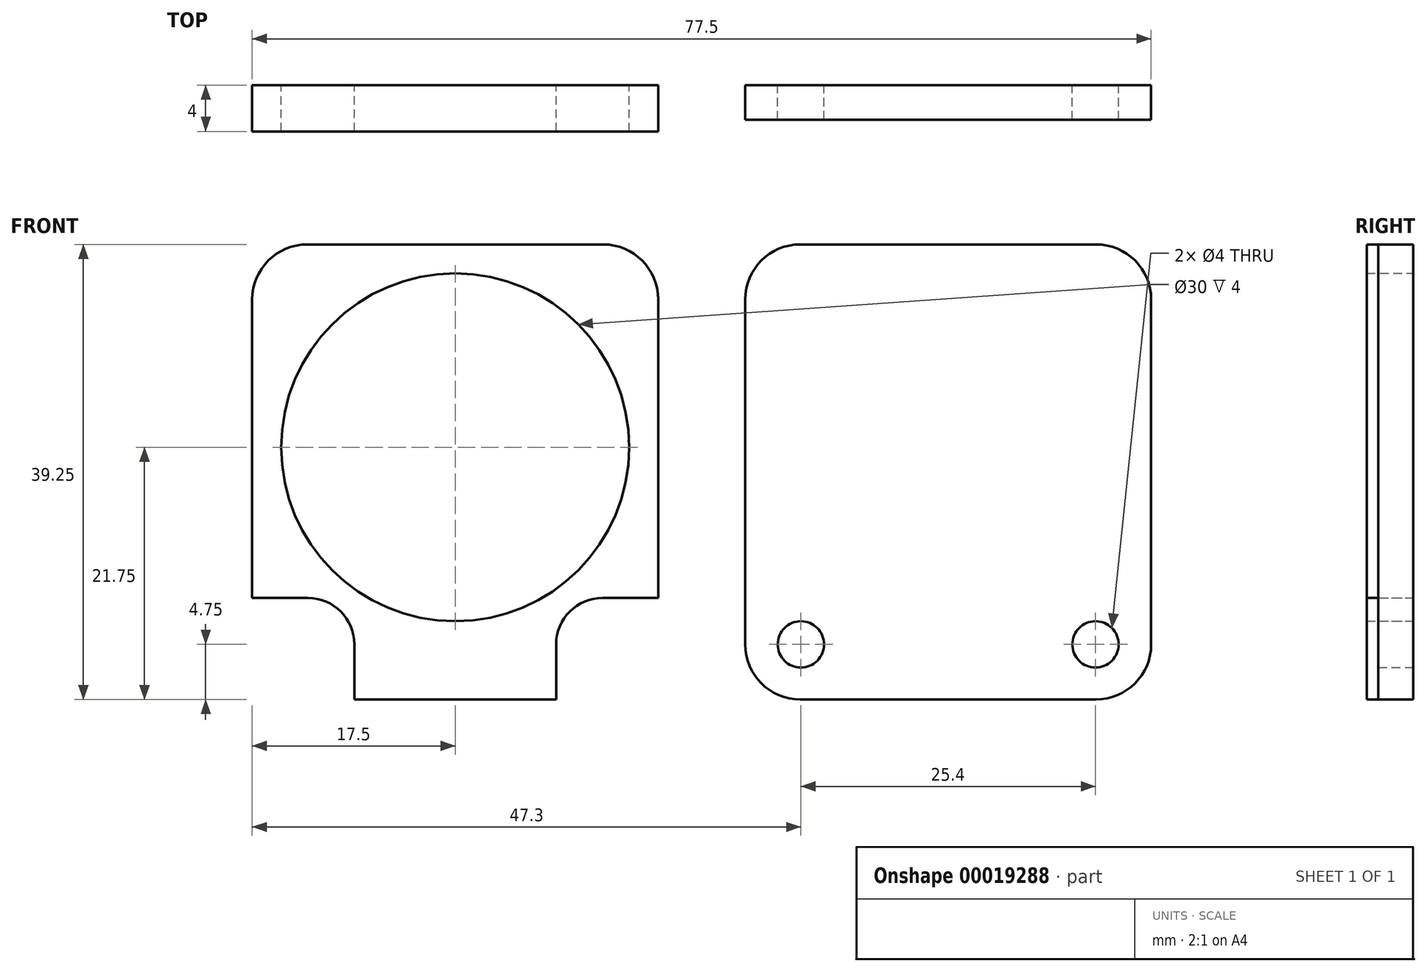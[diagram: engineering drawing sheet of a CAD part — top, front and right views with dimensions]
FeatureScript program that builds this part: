
annotation { "Feature Type Name" : "Feature", "Feature Type Description" : "" }
export const myFeature = defineFeature(function(context is Context, id is Id, definition is map)
    precondition{}
    {
        {
            var Q0;
            Q0=qCreatedBy(makeId("Front.planeOp"),FACE);
            var sketch = newSketch(context, id + "F0", { "sketchPlane" : qUnion([Q0])});
            skArc(sketch, "E0", {"start": v(12.7, 4) * mm, "mid": v(9.87, 2.83) * mm, "end": v(8.7, 0) * mm});
            skLineSegment(sketch, "E1", {"start": v(-12.7, 0) * mm, "end": v(12.7, 0) * mm, "construction": true});
            skLineSegment(sketch, "E2.bottom", {"start": v(-17.5, 2) * mm, "end": v(17.5, 2) * mm, "construction": true});
            skLineSegment(sketch, "E2.top", {"start": v(-17.5, -4.75) * mm, "end": v(-8.7, -4.75) * mm, "construction": true});
            skLineSegment(sketch, "E2.left", {"start": v(-17.5, 2) * mm, "end": v(-17.5, -4.75) * mm, "construction": true});
            skLineSegment(sketch, "E2.right", {"start": v(17.5, 2) * mm, "end": v(17.5, -4.75) * mm, "construction": true});
            skLineSegment(sketch, "E3", {"start": v(0, 2) * mm, "end": v(0, 0) * mm, "construction": true});
            skCircle(sketch, "E4", {"center": v(0, 17) * mm, "radius": 15 * mm});
            skLineSegment(sketch, "E5", {"start": v(-17.5, 2) * mm, "end": v(-17.5, 4) * mm, "construction": true});
            skLineSegment(sketch, "E6", {"start": v(-17.5, 34.5) * mm, "end": v(17.5, 34.5) * mm});
            skLineSegment(sketch, "E7", {"start": v(17.5, 34.5) * mm, "end": v(17.5, 4) * mm});
            skCircle(sketch, "E8", {"center": v(12.7, 0) * mm, "radius": 2.25 * mm, "construction": true});
            skCircle(sketch, "E9", {"center": v(-12.7, 0) * mm, "radius": 2.25 * mm, "construction": true});
            skCircle(sketch, "E10", {"center": v(12.7, 0) * mm, "radius": 4.75 * mm, "construction": true});
            skLineSegment(sketch, "E11", {"start": v(8.7, 0) * mm, "end": v(8.7, -4.75) * mm});
            skLineSegment(sketch, "E12", {"start": v(12.7, 4) * mm, "end": v(17.5, 4) * mm});
            skLineSegment(sketch, "E13", {"start": v(17.5, 4) * mm, "end": v(17.5, 2) * mm, "construction": true});
            skLineSegment(sketch, "E14", {"start": v(8.7, -4.75) * mm, "end": v(17.5, -4.75) * mm, "construction": true});
            skLineSegment(sketch, "E15.0.MirrorCS", {"start": v(-8.7, 0) * mm, "end": v(-8.7, -4.75) * mm});
            skLineSegment(sketch, "E15.1.MirrorCS", {"start": v(-12.7, 4) * mm, "end": v(-17.5, 4) * mm});
            skArc(sketch, "E15.2.MirrorCS", {"start": v(-12.7, 4) * mm, "mid": v(-9.87, 2.83) * mm, "end": v(-8.7, 0) * mm});
            skLineSegment(sketch, "E16", {"start": v(-17.5, 4) * mm, "end": v(-17.5, 34.5) * mm});
            skLineSegment(sketch, "E17", {"start": v(-8.7, -4.75) * mm, "end": v(8.7, -4.75) * mm});
            skSolve(sketch);
        }
        {
            var Q0;
            Q0=qSketchRegion(id+"F0",true);
            extrude(context, id + "F1", {"entities" : qUnion([Q0]), "depth" : 4 * mm});
        }
        {
            var Q0;
            Q0=qCreatedBy(makeId("Front.planeOp"),FACE);
            var sketch = newSketch(context, id + "F2", { "sketchPlane" : qUnion([Q0])});
            skLineSegment(sketch, "E18.bottom", {"start": v(25, -4.75) * mm, "end": v(60, -4.75) * mm});
            skLineSegment(sketch, "E18.top", {"start": v(25, 34.5) * mm, "end": v(60, 34.5) * mm});
            skLineSegment(sketch, "E18.left", {"start": v(25, -4.75) * mm, "end": v(25, 34.5) * mm});
            skLineSegment(sketch, "E18.right", {"start": v(60, -4.75) * mm, "end": v(60, 34.5) * mm});
            skCircle(sketch, "E19", {"center": v(29.8, 0) * mm, "radius": 2 * mm});
            skCircle(sketch, "E20", {"center": v(55.2, 0) * mm, "radius": 2 * mm});
            skLineSegment(sketch, "E21", {"start": v(42.5, -4.75) * mm, "end": v(42.5, 34.5) * mm, "construction": true});
            skLineSegment(sketch, "E22", {"start": v(29.8, 0) * mm, "end": v(42.5, 0) * mm, "construction": true});
            skLineSegment(sketch, "E23", {"start": v(42.5, 0) * mm, "end": v(55.2, 0) * mm, "construction": true});
            skSolve(sketch);
        }
        {
            var Q0;
            Q0=qSketchRegion(id+"F2",true);
            extrude(context, id + "F3", {"entities" : qUnion([Q0]), "depth" : 3 * mm});
        }
        {
            var Q0;
            Q0=makeQuery(id+"F1.opExtrude","SWEPT_EDGE",EDGE,{"disambiguationData":[OSD([sQuery(id+"F0.wireOp",EDGE,"E6"),sQuery(id+"F0.wireOp",EDGE,"E7")])]});
            var Q1;
            Q1=makeQuery(id+"F1.opExtrude","SWEPT_EDGE",EDGE,{"disambiguationData":[OSD([sQuery(id+"F0.wireOp",EDGE,"E5"),sQuery(id+"F0.wireOp",EDGE,"E6")])]});
            var Q2;
            Q2=makeQuery(id+"F1.opExtrude","SWEPT_EDGE",EDGE,{"disambiguationData":[OSD([sQuery(id+"F0.wireOp",EDGE,"E2.top"),sQuery(id+"F0.wireOp",EDGE,"E2.left")])]});
            var Q3;
            Q3=makeQuery(id+"F1.opExtrude","SWEPT_EDGE",EDGE,{"disambiguationData":[OSD([sQuery(id+"F0.wireOp",EDGE,"E2.top"),sQuery(id+"F0.wireOp",EDGE,"E2.right")])]});
            var Q4;
            Q4=makeQuery(id+"F3.opExtrude","SWEPT_EDGE",EDGE,{"disambiguationData":[OSD([sQuery(id+"F2.wireOp",EDGE,"E18.bottom"),sQuery(id+"F2.wireOp",EDGE,"E18.left")])]});
            var Q5;
            Q5=makeQuery(id+"F3.opExtrude","SWEPT_EDGE",EDGE,{"disambiguationData":[OSD([sQuery(id+"F2.wireOp",EDGE,"E18.bottom"),sQuery(id+"F2.wireOp",EDGE,"E18.right")])]});
            var Q6;
            Q6=makeQuery(id+"F3.opExtrude","SWEPT_EDGE",EDGE,{"disambiguationData":[OSD([sQuery(id+"F2.wireOp",EDGE,"E18.top"),sQuery(id+"F2.wireOp",EDGE,"E18.left")])]});
            var Q7;
            Q7=makeQuery(id+"F3.opExtrude","SWEPT_EDGE",EDGE,{"disambiguationData":[OSD([sQuery(id+"F2.wireOp",EDGE,"E18.top"),sQuery(id+"F2.wireOp",EDGE,"E18.right")])]});
            fillet(context, id + "F4", {"entities" : qUnion([Q0, Q1, Q2, Q3, Q4, Q5, Q6, Q7]), "radius" : 4.75 * mm, "tangentPropagation" : true, "allowEdgeOverflow" : false});
        }
    });
